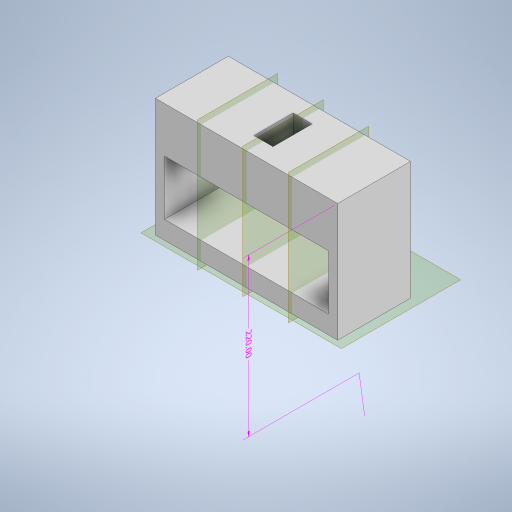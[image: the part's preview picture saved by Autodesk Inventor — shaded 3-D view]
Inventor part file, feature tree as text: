
AUTODESK INVENTOR PART (.ipt)
format: ipt  version: 2023 (Build 270158000, 158)  size: 317,952 bytes
history: native  units: mm
features: extrude x6, plane x6, sketch x6, other x5, split x1
ambient origin geometry x8: Origin, YZ Plane, XZ Plane, XY Plane, X Axis, Y Axis, Z Axis, Center Point
bodies: Body1 (feature_tree), Body2 (feature_tree)
feature tree (24):
  other  "Sólido1"
  other  "Anotaciones"
  extrude  "Extrusión1"  Depth=80.0mm
  extrude  "Extrusión2"  Depth=180.0mm
  extrude  "Extrusión3"  Depth=20.0mm
  extrude  "Extrusión4"  Depth=21.0mm
  plane  "Plano de trabajo1"
  extrude  "Extrusión6"  Depth=20.0mm
  plane  "Plano de trabajo3"
  extrude  "Extrusión7"  [1 undecoded]
  plane  "Plano de trabajo4"
  split  "Dividir1"
  other  "Suprimir cara4"
  plane  "Plano de trabajo5"
  plane  "Plano de trabajo6"
  plane  "Plano de trabajo7"
  sketch  "Boceto1"  dims[d0=200.0mm d1=80.0mm]
  sketch  "Boceto2"  dims[d2=130.0mm d3=0.0mm d4=180.0mm]
  sketch  "Boceto3"  dims[d5=60.0mm d6=20.0mm]
  sketch  "Boceto4"  dims[d7=60.0mm d8=0.0mm d9=21.0mm d10=43.0mm]
  sketch  "Boceto7"  dims[d11=43.0mm d12=0.0mm d13=20.0mm]
  other  "Sólido3"
  sketch  "Boceto10"  dims[d14=90.0mm d15=0.0mm d16=-90.0mm d28=20.0mm d29=20.0mm d30=30.0mm d31=30.0mm d32=20.0mm d33=35.0mm d34=35.0mm d35=69.0mm d36=10.0mm d37=0.0mm d45=1.5mm d50=10.0mm d51=0.0mm d52=10.0mm d53=89.5mm d54=90.0deg d38=3.166395mm d39=4.283575mm d40=220.0mm]
  other  "Cota lineal 1"
note: 1 required parameter value undecoded (feature->parameter linkage not recoverable at this tier; creation-order binding heuristic only, values carry confidence <= 0.55)
